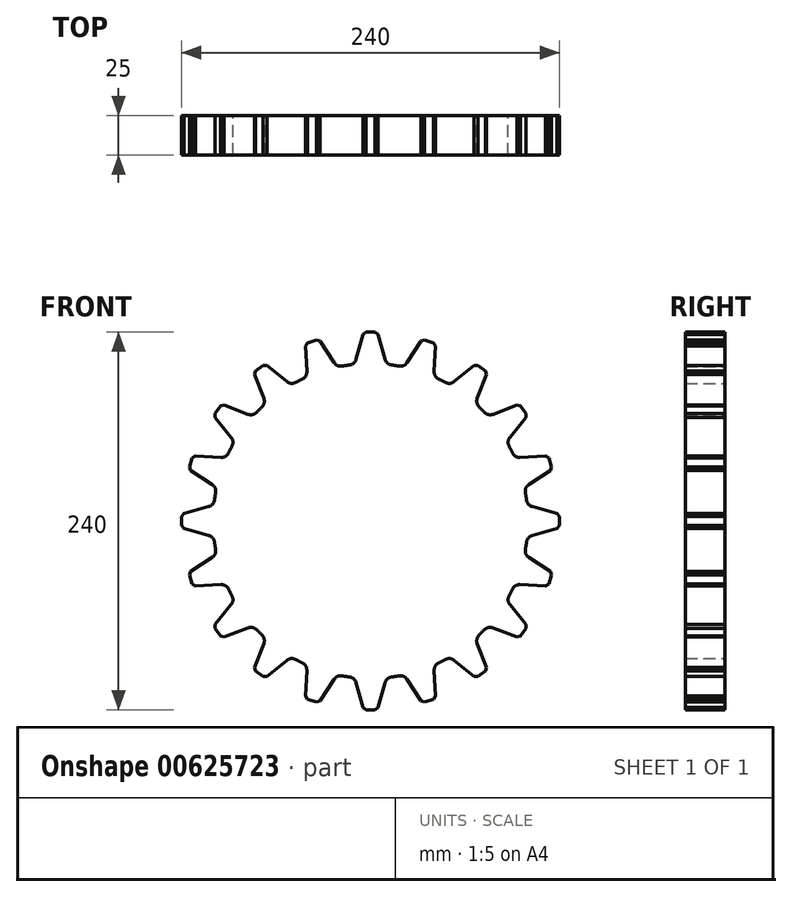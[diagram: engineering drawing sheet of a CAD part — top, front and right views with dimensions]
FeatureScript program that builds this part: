
annotation { "Feature Type Name" : "Feature", "Feature Type Description" : "" }
export const myFeature = defineFeature(function(context is Context, id is Id, definition is map)
    precondition{}
    {
        {
            var Q0;
            Q0=qCreatedBy(makeId("Front.planeOp"),FACE);
            var sketch = newSketch(context, id + "F0", { "sketchPlane" : qUnion([Q0])});
            skCircle(sketch, "E0", {"center": v(0, 0) * mm, "radius": 100 * mm});
            skCircle(sketch, "E1", {"center": v(0, 0) * mm, "radius": 120 * mm, "construction": true});
            skLineSegment(sketch, "E2", {"start": v(0, 120) * mm, "end": v(-4.5, 120) * mm});
            skLineSegment(sketch, "E3", {"start": v(0, 120) * mm, "end": v(4.5, 120) * mm});
            skLineSegment(sketch, "E4", {"start": v(4.5, 120) * mm, "end": v(10, 99.5) * mm});
            skLineSegment(sketch, "E5", {"start": v(-4.5, 120) * mm, "end": v(-10, 99.5) * mm});
            skLineSegment(sketch, "E6.anchor1", {"start": v(0, 0) * mm, "end": v(0, 120) * mm, "construction": true});
            skLineSegment(sketch, "E6.anchor2", {"start": v(0, 0) * mm, "end": v(0, 120) * mm, "construction": true});
            skLineSegment(sketch, "E7.1.0", {"start": v(-37.08, 114.13) * mm, "end": v(-41.36, 112.74) * mm});
            skLineSegment(sketch, "E7.1.1", {"start": v(-37.08, 114.13) * mm, "end": v(-32.8, 115.52) * mm});
            skLineSegment(sketch, "E7.1.2", {"start": v(-32.8, 115.52) * mm, "end": v(-21.24, 97.72) * mm});
            skLineSegment(sketch, "E7.1.3", {"start": v(-41.36, 112.74) * mm, "end": v(-40.25, 91.54) * mm});
            skLineSegment(sketch, "E7.2.0", {"start": v(-70.53, 97.08) * mm, "end": v(-74.17, 94.44) * mm});
            skLineSegment(sketch, "E7.2.1", {"start": v(-70.53, 97.08) * mm, "end": v(-66.9, 99.73) * mm});
            skLineSegment(sketch, "E7.2.2", {"start": v(-66.9, 99.73) * mm, "end": v(-50.4, 86.37) * mm});
            skLineSegment(sketch, "E7.2.3", {"start": v(-74.17, 94.44) * mm, "end": v(-66.57, 74.62) * mm});
            skLineSegment(sketch, "E7.3.0", {"start": v(-97.08, 70.53) * mm, "end": v(-99.73, 66.9) * mm});
            skLineSegment(sketch, "E7.3.1", {"start": v(-97.08, 70.53) * mm, "end": v(-94.44, 74.17) * mm});
            skLineSegment(sketch, "E7.3.2", {"start": v(-94.44, 74.17) * mm, "end": v(-74.62, 66.57) * mm});
            skLineSegment(sketch, "E7.3.3", {"start": v(-99.73, 66.9) * mm, "end": v(-86.37, 50.4) * mm});
            skLineSegment(sketch, "E7.4.0", {"start": v(-114.13, 37.08) * mm, "end": v(-115.52, 32.8) * mm});
            skLineSegment(sketch, "E7.4.1", {"start": v(-114.13, 37.08) * mm, "end": v(-112.74, 41.36) * mm});
            skLineSegment(sketch, "E7.4.2", {"start": v(-112.74, 41.36) * mm, "end": v(-91.54, 40.25) * mm});
            skLineSegment(sketch, "E7.4.3", {"start": v(-115.52, 32.8) * mm, "end": v(-97.72, 21.24) * mm});
            skLineSegment(sketch, "E7.5.0", {"start": v(-120, 0) * mm, "end": v(-120, -4.5) * mm});
            skLineSegment(sketch, "E7.5.1", {"start": v(-120, 0) * mm, "end": v(-120, 4.5) * mm});
            skLineSegment(sketch, "E7.5.2", {"start": v(-120, 4.5) * mm, "end": v(-99.5, 10) * mm});
            skLineSegment(sketch, "E7.5.3", {"start": v(-120, -4.5) * mm, "end": v(-99.5, -10) * mm});
            skLineSegment(sketch, "E7.6.0", {"start": v(-114.13, -37.08) * mm, "end": v(-112.74, -41.36) * mm});
            skLineSegment(sketch, "E7.6.1", {"start": v(-114.13, -37.08) * mm, "end": v(-115.52, -32.8) * mm});
            skLineSegment(sketch, "E7.6.2", {"start": v(-115.52, -32.8) * mm, "end": v(-97.72, -21.24) * mm});
            skLineSegment(sketch, "E7.6.3", {"start": v(-112.74, -41.36) * mm, "end": v(-91.54, -40.25) * mm});
            skLineSegment(sketch, "E7.7.0", {"start": v(-97.08, -70.53) * mm, "end": v(-94.44, -74.17) * mm});
            skLineSegment(sketch, "E7.7.1", {"start": v(-97.08, -70.53) * mm, "end": v(-99.73, -66.9) * mm});
            skLineSegment(sketch, "E7.7.2", {"start": v(-99.73, -66.9) * mm, "end": v(-86.37, -50.4) * mm});
            skLineSegment(sketch, "E7.7.3", {"start": v(-94.44, -74.17) * mm, "end": v(-74.62, -66.57) * mm});
            skLineSegment(sketch, "E7.8.0", {"start": v(-70.53, -97.08) * mm, "end": v(-66.9, -99.73) * mm});
            skLineSegment(sketch, "E7.8.1", {"start": v(-70.53, -97.08) * mm, "end": v(-74.17, -94.44) * mm});
            skLineSegment(sketch, "E7.8.2", {"start": v(-74.17, -94.44) * mm, "end": v(-66.57, -74.62) * mm});
            skLineSegment(sketch, "E7.8.3", {"start": v(-66.9, -99.73) * mm, "end": v(-50.4, -86.37) * mm});
            skLineSegment(sketch, "E7.9.0", {"start": v(-37.08, -114.13) * mm, "end": v(-32.8, -115.52) * mm});
            skLineSegment(sketch, "E7.9.1", {"start": v(-37.08, -114.13) * mm, "end": v(-41.36, -112.74) * mm});
            skLineSegment(sketch, "E7.9.2", {"start": v(-41.36, -112.74) * mm, "end": v(-40.25, -91.54) * mm});
            skLineSegment(sketch, "E7.9.3", {"start": v(-32.8, -115.52) * mm, "end": v(-21.24, -97.72) * mm});
            skLineSegment(sketch, "E7.10.0", {"start": v(0, -120) * mm, "end": v(4.5, -120) * mm});
            skLineSegment(sketch, "E7.10.1", {"start": v(0, -120) * mm, "end": v(-4.5, -120) * mm});
            skLineSegment(sketch, "E7.10.2", {"start": v(-4.5, -120) * mm, "end": v(-10, -99.5) * mm});
            skLineSegment(sketch, "E7.10.3", {"start": v(4.5, -120) * mm, "end": v(10, -99.5) * mm});
            skLineSegment(sketch, "E7.11.0", {"start": v(37.08, -114.13) * mm, "end": v(41.36, -112.74) * mm});
            skLineSegment(sketch, "E7.11.1", {"start": v(37.08, -114.13) * mm, "end": v(32.8, -115.52) * mm});
            skLineSegment(sketch, "E7.11.2", {"start": v(32.8, -115.52) * mm, "end": v(21.24, -97.72) * mm});
            skLineSegment(sketch, "E7.11.3", {"start": v(41.36, -112.74) * mm, "end": v(40.25, -91.54) * mm});
            skLineSegment(sketch, "E7.12.0", {"start": v(70.53, -97.08) * mm, "end": v(74.17, -94.44) * mm});
            skLineSegment(sketch, "E7.12.1", {"start": v(70.53, -97.08) * mm, "end": v(66.9, -99.73) * mm});
            skLineSegment(sketch, "E7.12.2", {"start": v(66.9, -99.73) * mm, "end": v(50.4, -86.37) * mm});
            skLineSegment(sketch, "E7.12.3", {"start": v(74.17, -94.44) * mm, "end": v(66.57, -74.62) * mm});
            skLineSegment(sketch, "E7.13.0", {"start": v(97.08, -70.53) * mm, "end": v(99.73, -66.9) * mm});
            skLineSegment(sketch, "E7.13.1", {"start": v(97.08, -70.53) * mm, "end": v(94.44, -74.17) * mm});
            skLineSegment(sketch, "E7.13.2", {"start": v(94.44, -74.17) * mm, "end": v(74.62, -66.57) * mm});
            skLineSegment(sketch, "E7.13.3", {"start": v(99.73, -66.9) * mm, "end": v(86.37, -50.4) * mm});
            skLineSegment(sketch, "E7.14.0", {"start": v(114.13, -37.08) * mm, "end": v(115.52, -32.8) * mm});
            skLineSegment(sketch, "E7.14.1", {"start": v(114.13, -37.08) * mm, "end": v(112.74, -41.36) * mm});
            skLineSegment(sketch, "E7.14.2", {"start": v(112.74, -41.36) * mm, "end": v(91.54, -40.25) * mm});
            skLineSegment(sketch, "E7.14.3", {"start": v(115.52, -32.8) * mm, "end": v(97.72, -21.24) * mm});
            skLineSegment(sketch, "E7.15.0", {"start": v(120, 0) * mm, "end": v(120, 4.5) * mm});
            skLineSegment(sketch, "E7.15.1", {"start": v(120, 0) * mm, "end": v(120, -4.5) * mm});
            skLineSegment(sketch, "E7.15.2", {"start": v(120, -4.5) * mm, "end": v(99.5, -10) * mm});
            skLineSegment(sketch, "E7.15.3", {"start": v(120, 4.5) * mm, "end": v(99.5, 10) * mm});
            skLineSegment(sketch, "E7.16.0", {"start": v(114.13, 37.08) * mm, "end": v(112.74, 41.36) * mm});
            skLineSegment(sketch, "E7.16.1", {"start": v(114.13, 37.08) * mm, "end": v(115.52, 32.8) * mm});
            skLineSegment(sketch, "E7.16.2", {"start": v(115.52, 32.8) * mm, "end": v(97.72, 21.24) * mm});
            skLineSegment(sketch, "E7.16.3", {"start": v(112.74, 41.36) * mm, "end": v(91.54, 40.25) * mm});
            skLineSegment(sketch, "E7.17.0", {"start": v(97.08, 70.53) * mm, "end": v(94.44, 74.17) * mm});
            skLineSegment(sketch, "E7.17.1", {"start": v(97.08, 70.53) * mm, "end": v(99.73, 66.9) * mm});
            skLineSegment(sketch, "E7.17.2", {"start": v(99.73, 66.9) * mm, "end": v(86.37, 50.4) * mm});
            skLineSegment(sketch, "E7.17.3", {"start": v(94.44, 74.17) * mm, "end": v(74.62, 66.57) * mm});
            skLineSegment(sketch, "E7.18.0", {"start": v(70.53, 97.08) * mm, "end": v(66.9, 99.73) * mm});
            skLineSegment(sketch, "E7.18.1", {"start": v(70.53, 97.08) * mm, "end": v(74.17, 94.44) * mm});
            skLineSegment(sketch, "E7.18.2", {"start": v(74.17, 94.44) * mm, "end": v(66.57, 74.62) * mm});
            skLineSegment(sketch, "E7.18.3", {"start": v(66.9, 99.73) * mm, "end": v(50.4, 86.37) * mm});
            skLineSegment(sketch, "E7.19.0", {"start": v(37.08, 114.13) * mm, "end": v(32.8, 115.52) * mm});
            skLineSegment(sketch, "E7.19.1", {"start": v(37.08, 114.13) * mm, "end": v(41.36, 112.74) * mm});
            skLineSegment(sketch, "E7.19.2", {"start": v(41.36, 112.74) * mm, "end": v(40.25, 91.54) * mm});
            skLineSegment(sketch, "E7.19.3", {"start": v(32.8, 115.52) * mm, "end": v(21.24, 97.72) * mm});
            skSolve(sketch);
        }
        {
            var Q0;
            {var subQ0=sQuery(id+"F0.wireOp",EDGE,"E0");var subQ18=makeQuery(id+"F0.imprint","INTERSECT",VERTEX,{"derivedFrom":[subQ0,sQuery(id+"F0.wireOp",EDGE,"E7.15.3")]});Q0=makeQuery(id+"F0.imprint","IMPRINT",FACE,{"disambiguationData":[TD([[makeQuery(id+"F0.imprint","IMPRINT",EDGE,{"disambiguationData":[TD([[subQ18,-1.0]])],"derivedFrom":subQ0}),1.0]])]});}
            var Q1;
            Q1=makeQuery(id+"F0.imprint","IMPRINT",FACE,{"disambiguationData":[TD([[makeQuery(id+"F0.imprint","IMPRINT",EDGE,{"derivedFrom":sQuery(id+"F0.wireOp",EDGE,"E7.1.0")}),1.0]])]});
            var Q2;
            Q2=makeQuery(id+"F0.imprint","IMPRINT",FACE,{"disambiguationData":[TD([[makeQuery(id+"F0.imprint","IMPRINT",EDGE,{"derivedFrom":sQuery(id+"F0.wireOp",EDGE,"E3")}),-1.0]])]});
            var Q3;
            Q3=makeQuery(id+"F0.imprint","IMPRINT",FACE,{"disambiguationData":[TD([[makeQuery(id+"F0.imprint","IMPRINT",EDGE,{"derivedFrom":sQuery(id+"F0.wireOp",EDGE,"E7.19.0")}),1.0]])]});
            var Q4;
            Q4=makeQuery(id+"F0.imprint","IMPRINT",FACE,{"disambiguationData":[TD([[makeQuery(id+"F0.imprint","IMPRINT",EDGE,{"derivedFrom":sQuery(id+"F0.wireOp",EDGE,"E7.18.0")}),1.0]])]});
            var Q5;
            Q5=makeQuery(id+"F0.imprint","IMPRINT",FACE,{"disambiguationData":[TD([[makeQuery(id+"F0.imprint","IMPRINT",EDGE,{"derivedFrom":sQuery(id+"F0.wireOp",EDGE,"E7.17.0")}),1.0]])]});
            var Q6;
            Q6=makeQuery(id+"F0.imprint","IMPRINT",FACE,{"disambiguationData":[TD([[makeQuery(id+"F0.imprint","IMPRINT",EDGE,{"derivedFrom":sQuery(id+"F0.wireOp",EDGE,"E7.16.0")}),1.0]])]});
            var Q7;
            Q7=makeQuery(id+"F0.imprint","IMPRINT",FACE,{"disambiguationData":[TD([[makeQuery(id+"F0.imprint","IMPRINT",EDGE,{"derivedFrom":sQuery(id+"F0.wireOp",EDGE,"E7.15.0")}),1.0]])]});
            var Q8;
            Q8=makeQuery(id+"F0.imprint","IMPRINT",FACE,{"disambiguationData":[TD([[makeQuery(id+"F0.imprint","IMPRINT",EDGE,{"derivedFrom":sQuery(id+"F0.wireOp",EDGE,"E7.14.0")}),1.0]])]});
            var Q9;
            Q9=makeQuery(id+"F0.imprint","IMPRINT",FACE,{"disambiguationData":[TD([[makeQuery(id+"F0.imprint","IMPRINT",EDGE,{"derivedFrom":sQuery(id+"F0.wireOp",EDGE,"E7.13.0")}),1.0]])]});
            var Q10;
            Q10=makeQuery(id+"F0.imprint","IMPRINT",FACE,{"disambiguationData":[TD([[makeQuery(id+"F0.imprint","IMPRINT",EDGE,{"derivedFrom":sQuery(id+"F0.wireOp",EDGE,"E7.12.0")}),1.0]])]});
            var Q11;
            Q11=makeQuery(id+"F0.imprint","IMPRINT",FACE,{"disambiguationData":[TD([[makeQuery(id+"F0.imprint","IMPRINT",EDGE,{"derivedFrom":sQuery(id+"F0.wireOp",EDGE,"E7.11.0")}),1.0]])]});
            var Q12;
            Q12=makeQuery(id+"F0.imprint","IMPRINT",FACE,{"disambiguationData":[TD([[makeQuery(id+"F0.imprint","IMPRINT",EDGE,{"derivedFrom":sQuery(id+"F0.wireOp",EDGE,"E7.10.0")}),1.0]])]});
            var Q13;
            Q13=makeQuery(id+"F0.imprint","IMPRINT",FACE,{"disambiguationData":[TD([[makeQuery(id+"F0.imprint","IMPRINT",EDGE,{"derivedFrom":sQuery(id+"F0.wireOp",EDGE,"E7.9.0")}),1.0]])]});
            var Q14;
            Q14=makeQuery(id+"F0.imprint","IMPRINT",FACE,{"disambiguationData":[TD([[makeQuery(id+"F0.imprint","IMPRINT",EDGE,{"derivedFrom":sQuery(id+"F0.wireOp",EDGE,"E7.8.0")}),1.0]])]});
            var Q15;
            Q15=makeQuery(id+"F0.imprint","IMPRINT",FACE,{"disambiguationData":[TD([[makeQuery(id+"F0.imprint","IMPRINT",EDGE,{"derivedFrom":sQuery(id+"F0.wireOp",EDGE,"E7.7.0")}),1.0]])]});
            var Q16;
            Q16=makeQuery(id+"F0.imprint","IMPRINT",FACE,{"disambiguationData":[TD([[makeQuery(id+"F0.imprint","IMPRINT",EDGE,{"derivedFrom":sQuery(id+"F0.wireOp",EDGE,"E7.6.0")}),1.0]])]});
            var Q17;
            Q17=makeQuery(id+"F0.imprint","IMPRINT",FACE,{"disambiguationData":[TD([[makeQuery(id+"F0.imprint","IMPRINT",EDGE,{"derivedFrom":sQuery(id+"F0.wireOp",EDGE,"E7.5.0")}),1.0]])]});
            var Q18;
            Q18=makeQuery(id+"F0.imprint","IMPRINT",FACE,{"disambiguationData":[TD([[makeQuery(id+"F0.imprint","IMPRINT",EDGE,{"derivedFrom":sQuery(id+"F0.wireOp",EDGE,"E7.4.0")}),1.0]])]});
            var Q19;
            Q19=makeQuery(id+"F0.imprint","IMPRINT",FACE,{"disambiguationData":[TD([[makeQuery(id+"F0.imprint","IMPRINT",EDGE,{"derivedFrom":sQuery(id+"F0.wireOp",EDGE,"E7.3.0")}),1.0]])]});
            var Q20;
            Q20=makeQuery(id+"F0.imprint","IMPRINT",FACE,{"disambiguationData":[TD([[makeQuery(id+"F0.imprint","IMPRINT",EDGE,{"derivedFrom":sQuery(id+"F0.wireOp",EDGE,"E7.2.0")}),1.0]])]});
            extrude(context, id + "F1", {"entities" : qUnion([Q0, Q1, Q2, Q3, Q4, Q5, Q6, Q7, Q8, Q9, Q10, Q11, Q12, Q13, Q14, Q15, Q16, Q17, Q18, Q19, Q20]), "endBound" : BoundingType.SYMMETRIC, "depth" : 25 * mm, "offsetDistance" : 25 * mm});
        }
        {
            var Q0;
            Q0=makeQuery(id+"F1.opExtrude","SWEPT_EDGE",EDGE,{"disambiguationData":[OSD([sQuery(id+"F0.wireOp",EDGE,"E7.15.1"),sQuery(id+"F0.wireOp",EDGE,"E7.15.2")])]});
            var Q1;
            Q1=makeQuery(id+"F1.opExtrude","SWEPT_EDGE",EDGE,{"disambiguationData":[OSD([sQuery(id+"F0.wireOp",EDGE,"E7.15.0"),sQuery(id+"F0.wireOp",EDGE,"E7.15.3")])]});
            chamfer(context, id + "F2", {"entities" : qUnion([Q0, Q1]), "width" : 2 * mm, "tangentPropagation" : true});
        }
        {
            var Q0;
            Q0=makeQuery(id+"F1.opExtrude","SWEPT_EDGE",EDGE,{"disambiguationData":[OSD([sQuery(id+"F0.wireOp",EDGE,"E0"),sQuery(id+"F0.wireOp",EDGE,"E7.15.3")])]});
            var Q1;
            Q1=makeQuery(id+"F1.opExtrude","SWEPT_EDGE",EDGE,{"disambiguationData":[OSD([sQuery(id+"F0.wireOp",EDGE,"E0"),sQuery(id+"F0.wireOp",EDGE,"E7.16.2")])]});
            fillet(context, id + "F3", {"entities" : qUnion([Q0, Q1]), "radius" : 5 * mm, "tangentPropagation" : true, "allowEdgeOverflow" : false});
        }
        {
            var Q0;
            Q0=makeQuery(id+"F1.opExtrude","SWEPT_EDGE",EDGE,{"disambiguationData":[OSD([sQuery(id+"F0.wireOp",EDGE,"E7.14.0"),sQuery(id+"F0.wireOp",EDGE,"E7.14.3")])]});
            var Q1;
            Q1=makeQuery(id+"F1.opExtrude","SWEPT_EDGE",EDGE,{"disambiguationData":[OSD([sQuery(id+"F0.wireOp",EDGE,"E7.14.1"),sQuery(id+"F0.wireOp",EDGE,"E7.14.2")])]});
            var Q2;
            Q2=makeQuery(id+"F1.opExtrude","SWEPT_EDGE",EDGE,{"disambiguationData":[OSD([sQuery(id+"F0.wireOp",EDGE,"E7.13.0"),sQuery(id+"F0.wireOp",EDGE,"E7.13.3")])]});
            var Q3;
            Q3=makeQuery(id+"F1.opExtrude","SWEPT_EDGE",EDGE,{"disambiguationData":[OSD([sQuery(id+"F0.wireOp",EDGE,"E7.13.1"),sQuery(id+"F0.wireOp",EDGE,"E7.13.2")])]});
            var Q4;
            Q4=makeQuery(id+"F1.opExtrude","SWEPT_EDGE",EDGE,{"disambiguationData":[OSD([sQuery(id+"F0.wireOp",EDGE,"E7.12.0"),sQuery(id+"F0.wireOp",EDGE,"E7.12.3")])]});
            var Q5;
            Q5=makeQuery(id+"F1.opExtrude","SWEPT_EDGE",EDGE,{"disambiguationData":[OSD([sQuery(id+"F0.wireOp",EDGE,"E7.12.1"),sQuery(id+"F0.wireOp",EDGE,"E7.12.2")])]});
            var Q6;
            Q6=makeQuery(id+"F1.opExtrude","SWEPT_EDGE",EDGE,{"disambiguationData":[OSD([sQuery(id+"F0.wireOp",EDGE,"E7.11.0"),sQuery(id+"F0.wireOp",EDGE,"E7.11.3")])]});
            var Q7;
            Q7=makeQuery(id+"F1.opExtrude","SWEPT_EDGE",EDGE,{"disambiguationData":[OSD([sQuery(id+"F0.wireOp",EDGE,"E7.11.1"),sQuery(id+"F0.wireOp",EDGE,"E7.11.2")])]});
            var Q8;
            Q8=makeQuery(id+"F1.opExtrude","SWEPT_EDGE",EDGE,{"disambiguationData":[OSD([sQuery(id+"F0.wireOp",EDGE,"E7.10.0"),sQuery(id+"F0.wireOp",EDGE,"E7.10.3")])]});
            var Q9;
            Q9=makeQuery(id+"F1.opExtrude","SWEPT_EDGE",EDGE,{"disambiguationData":[OSD([sQuery(id+"F0.wireOp",EDGE,"E7.10.1"),sQuery(id+"F0.wireOp",EDGE,"E7.10.2")])]});
            var Q10;
            Q10=makeQuery(id+"F1.opExtrude","SWEPT_EDGE",EDGE,{"disambiguationData":[OSD([sQuery(id+"F0.wireOp",EDGE,"E7.9.0"),sQuery(id+"F0.wireOp",EDGE,"E7.9.3")])]});
            var Q11;
            Q11=makeQuery(id+"F1.opExtrude","SWEPT_EDGE",EDGE,{"disambiguationData":[OSD([sQuery(id+"F0.wireOp",EDGE,"E7.9.1"),sQuery(id+"F0.wireOp",EDGE,"E7.9.2")])]});
            var Q12;
            Q12=makeQuery(id+"F1.opExtrude","SWEPT_EDGE",EDGE,{"disambiguationData":[OSD([sQuery(id+"F0.wireOp",EDGE,"E7.8.0"),sQuery(id+"F0.wireOp",EDGE,"E7.8.3")])]});
            var Q13;
            Q13=makeQuery(id+"F1.opExtrude","SWEPT_EDGE",EDGE,{"disambiguationData":[OSD([sQuery(id+"F0.wireOp",EDGE,"E7.8.1"),sQuery(id+"F0.wireOp",EDGE,"E7.8.2")])]});
            var Q14;
            Q14=makeQuery(id+"F1.opExtrude","SWEPT_EDGE",EDGE,{"disambiguationData":[OSD([sQuery(id+"F0.wireOp",EDGE,"E7.7.0"),sQuery(id+"F0.wireOp",EDGE,"E7.7.3")])]});
            var Q15;
            Q15=makeQuery(id+"F1.opExtrude","SWEPT_EDGE",EDGE,{"disambiguationData":[OSD([sQuery(id+"F0.wireOp",EDGE,"E7.7.1"),sQuery(id+"F0.wireOp",EDGE,"E7.7.2")])]});
            var Q16;
            Q16=makeQuery(id+"F1.opExtrude","SWEPT_EDGE",EDGE,{"disambiguationData":[OSD([sQuery(id+"F0.wireOp",EDGE,"E7.6.0"),sQuery(id+"F0.wireOp",EDGE,"E7.6.3")])]});
            var Q17;
            Q17=makeQuery(id+"F1.opExtrude","SWEPT_EDGE",EDGE,{"disambiguationData":[OSD([sQuery(id+"F0.wireOp",EDGE,"E7.6.1"),sQuery(id+"F0.wireOp",EDGE,"E7.6.2")])]});
            var Q18;
            Q18=makeQuery(id+"F1.opExtrude","SWEPT_EDGE",EDGE,{"disambiguationData":[OSD([sQuery(id+"F0.wireOp",EDGE,"E7.5.0"),sQuery(id+"F0.wireOp",EDGE,"E7.5.3")])]});
            var Q19;
            Q19=makeQuery(id+"F1.opExtrude","SWEPT_EDGE",EDGE,{"disambiguationData":[OSD([sQuery(id+"F0.wireOp",EDGE,"E7.5.1"),sQuery(id+"F0.wireOp",EDGE,"E7.5.2")])]});
            var Q20;
            Q20=makeQuery(id+"F1.opExtrude","SWEPT_EDGE",EDGE,{"disambiguationData":[OSD([sQuery(id+"F0.wireOp",EDGE,"E7.4.0"),sQuery(id+"F0.wireOp",EDGE,"E7.4.3")])]});
            var Q21;
            Q21=makeQuery(id+"F1.opExtrude","SWEPT_EDGE",EDGE,{"disambiguationData":[OSD([sQuery(id+"F0.wireOp",EDGE,"E7.4.1"),sQuery(id+"F0.wireOp",EDGE,"E7.4.2")])]});
            var Q22;
            Q22=makeQuery(id+"F1.opExtrude","SWEPT_EDGE",EDGE,{"disambiguationData":[OSD([sQuery(id+"F0.wireOp",EDGE,"E7.3.0"),sQuery(id+"F0.wireOp",EDGE,"E7.3.3")])]});
            var Q23;
            Q23=makeQuery(id+"F1.opExtrude","SWEPT_EDGE",EDGE,{"disambiguationData":[OSD([sQuery(id+"F0.wireOp",EDGE,"E7.3.1"),sQuery(id+"F0.wireOp",EDGE,"E7.3.2")])]});
            var Q24;
            Q24=makeQuery(id+"F1.opExtrude","SWEPT_EDGE",EDGE,{"disambiguationData":[OSD([sQuery(id+"F0.wireOp",EDGE,"E7.2.0"),sQuery(id+"F0.wireOp",EDGE,"E7.2.3")])]});
            var Q25;
            Q25=makeQuery(id+"F1.opExtrude","SWEPT_EDGE",EDGE,{"disambiguationData":[OSD([sQuery(id+"F0.wireOp",EDGE,"E7.2.1"),sQuery(id+"F0.wireOp",EDGE,"E7.2.2")])]});
            var Q26;
            Q26=makeQuery(id+"F1.opExtrude","SWEPT_EDGE",EDGE,{"disambiguationData":[OSD([sQuery(id+"F0.wireOp",EDGE,"E7.1.0"),sQuery(id+"F0.wireOp",EDGE,"E7.1.3")])]});
            var Q27;
            Q27=makeQuery(id+"F1.opExtrude","SWEPT_EDGE",EDGE,{"disambiguationData":[OSD([sQuery(id+"F0.wireOp",EDGE,"E7.1.1"),sQuery(id+"F0.wireOp",EDGE,"E7.1.2")])]});
            var Q28;
            Q28=makeQuery(id+"F1.opExtrude","SWEPT_EDGE",EDGE,{"disambiguationData":[OSD([sQuery(id+"F0.wireOp",EDGE,"E2"),sQuery(id+"F0.wireOp",EDGE,"E5")])]});
            var Q29;
            Q29=makeQuery(id+"F1.opExtrude","SWEPT_EDGE",EDGE,{"disambiguationData":[OSD([sQuery(id+"F0.wireOp",EDGE,"E3"),sQuery(id+"F0.wireOp",EDGE,"E4")])]});
            var Q30;
            Q30=makeQuery(id+"F1.opExtrude","SWEPT_EDGE",EDGE,{"disambiguationData":[OSD([sQuery(id+"F0.wireOp",EDGE,"E7.19.0"),sQuery(id+"F0.wireOp",EDGE,"E7.19.3")])]});
            var Q31;
            Q31=makeQuery(id+"F1.opExtrude","SWEPT_EDGE",EDGE,{"disambiguationData":[OSD([sQuery(id+"F0.wireOp",EDGE,"E7.19.1"),sQuery(id+"F0.wireOp",EDGE,"E7.19.2")])]});
            var Q32;
            Q32=makeQuery(id+"F1.opExtrude","SWEPT_EDGE",EDGE,{"disambiguationData":[OSD([sQuery(id+"F0.wireOp",EDGE,"E7.18.0"),sQuery(id+"F0.wireOp",EDGE,"E7.18.3")])]});
            var Q33;
            Q33=makeQuery(id+"F1.opExtrude","SWEPT_EDGE",EDGE,{"disambiguationData":[OSD([sQuery(id+"F0.wireOp",EDGE,"E7.18.1"),sQuery(id+"F0.wireOp",EDGE,"E7.18.2")])]});
            var Q34;
            Q34=makeQuery(id+"F1.opExtrude","SWEPT_EDGE",EDGE,{"disambiguationData":[OSD([sQuery(id+"F0.wireOp",EDGE,"E7.17.0"),sQuery(id+"F0.wireOp",EDGE,"E7.17.3")])]});
            var Q35;
            Q35=makeQuery(id+"F1.opExtrude","SWEPT_EDGE",EDGE,{"disambiguationData":[OSD([sQuery(id+"F0.wireOp",EDGE,"E7.17.1"),sQuery(id+"F0.wireOp",EDGE,"E7.17.2")])]});
            var Q36;
            Q36=makeQuery(id+"F1.opExtrude","SWEPT_EDGE",EDGE,{"disambiguationData":[OSD([sQuery(id+"F0.wireOp",EDGE,"E7.16.0"),sQuery(id+"F0.wireOp",EDGE,"E7.16.3")])]});
            var Q37;
            Q37=makeQuery(id+"F1.opExtrude","SWEPT_EDGE",EDGE,{"disambiguationData":[OSD([sQuery(id+"F0.wireOp",EDGE,"E7.16.1"),sQuery(id+"F0.wireOp",EDGE,"E7.16.2")])]});
            chamfer(context, id + "F4", {"entities" : qUnion([Q0, Q1, Q2, Q3, Q4, Q5, Q6, Q7, Q8, Q9, Q10, Q11, Q12, Q13, Q14, Q15, Q16, Q17, Q18, Q19, Q20, Q21, Q22, Q23, Q24, Q25, Q26, Q27, Q28, Q29, Q30, Q31, Q32, Q33, Q34, Q35, Q36, Q37]), "width" : 2 * mm, "tangentPropagation" : true});
        }
        {
            var Q0;
            Q0=makeQuery(id+"F1.opExtrude","SWEPT_EDGE",EDGE,{"disambiguationData":[OSD([sQuery(id+"F0.wireOp",EDGE,"E0"),sQuery(id+"F0.wireOp",EDGE,"E7.17.2")])]});
            var Q1;
            Q1=makeQuery(id+"F1.opExtrude","SWEPT_EDGE",EDGE,{"disambiguationData":[OSD([sQuery(id+"F0.wireOp",EDGE,"E0"),sQuery(id+"F0.wireOp",EDGE,"E7.16.3")])]});
            var Q2;
            Q2=makeQuery(id+"F1.opExtrude","SWEPT_EDGE",EDGE,{"disambiguationData":[OSD([sQuery(id+"F0.wireOp",EDGE,"E0"),sQuery(id+"F0.wireOp",EDGE,"E7.15.2")])]});
            var Q3;
            Q3=makeQuery(id+"F1.opExtrude","SWEPT_EDGE",EDGE,{"disambiguationData":[OSD([sQuery(id+"F0.wireOp",EDGE,"E0"),sQuery(id+"F0.wireOp",EDGE,"E7.14.3")])]});
            var Q4;
            Q4=makeQuery(id+"F1.opExtrude","SWEPT_EDGE",EDGE,{"disambiguationData":[OSD([sQuery(id+"F0.wireOp",EDGE,"E0"),sQuery(id+"F0.wireOp",EDGE,"E7.14.2")])]});
            var Q5;
            Q5=makeQuery(id+"F1.opExtrude","SWEPT_EDGE",EDGE,{"disambiguationData":[OSD([sQuery(id+"F0.wireOp",EDGE,"E0"),sQuery(id+"F0.wireOp",EDGE,"E7.13.3")])]});
            var Q6;
            Q6=makeQuery(id+"F1.opExtrude","SWEPT_EDGE",EDGE,{"disambiguationData":[OSD([sQuery(id+"F0.wireOp",EDGE,"E0"),sQuery(id+"F0.wireOp",EDGE,"E7.13.2")])]});
            var Q7;
            Q7=makeQuery(id+"F1.opExtrude","SWEPT_EDGE",EDGE,{"disambiguationData":[OSD([sQuery(id+"F0.wireOp",EDGE,"E0"),sQuery(id+"F0.wireOp",EDGE,"E7.12.3")])]});
            var Q8;
            Q8=makeQuery(id+"F1.opExtrude","SWEPT_EDGE",EDGE,{"disambiguationData":[OSD([sQuery(id+"F0.wireOp",EDGE,"E0"),sQuery(id+"F0.wireOp",EDGE,"E7.12.2")])]});
            var Q9;
            Q9=makeQuery(id+"F1.opExtrude","SWEPT_EDGE",EDGE,{"disambiguationData":[OSD([sQuery(id+"F0.wireOp",EDGE,"E0"),sQuery(id+"F0.wireOp",EDGE,"E7.11.3")])]});
            var Q10;
            Q10=makeQuery(id+"F1.opExtrude","SWEPT_EDGE",EDGE,{"disambiguationData":[OSD([sQuery(id+"F0.wireOp",EDGE,"E0"),sQuery(id+"F0.wireOp",EDGE,"E7.10.2")])]});
            var Q11;
            Q11=makeQuery(id+"F1.opExtrude","SWEPT_EDGE",EDGE,{"disambiguationData":[OSD([sQuery(id+"F0.wireOp",EDGE,"E0"),sQuery(id+"F0.wireOp",EDGE,"E7.9.3")])]});
            var Q12;
            Q12=makeQuery(id+"F1.opExtrude","SWEPT_EDGE",EDGE,{"disambiguationData":[OSD([sQuery(id+"F0.wireOp",EDGE,"E0"),sQuery(id+"F0.wireOp",EDGE,"E7.9.2")])]});
            var Q13;
            Q13=makeQuery(id+"F1.opExtrude","SWEPT_EDGE",EDGE,{"disambiguationData":[OSD([sQuery(id+"F0.wireOp",EDGE,"E0"),sQuery(id+"F0.wireOp",EDGE,"E7.8.3")])]});
            var Q14;
            Q14=makeQuery(id+"F1.opExtrude","SWEPT_EDGE",EDGE,{"disambiguationData":[OSD([sQuery(id+"F0.wireOp",EDGE,"E0"),sQuery(id+"F0.wireOp",EDGE,"E7.8.2")])]});
            var Q15;
            Q15=makeQuery(id+"F1.opExtrude","SWEPT_EDGE",EDGE,{"disambiguationData":[OSD([sQuery(id+"F0.wireOp",EDGE,"E0"),sQuery(id+"F0.wireOp",EDGE,"E7.7.3")])]});
            var Q16;
            Q16=makeQuery(id+"F1.opExtrude","SWEPT_EDGE",EDGE,{"disambiguationData":[OSD([sQuery(id+"F0.wireOp",EDGE,"E0"),sQuery(id+"F0.wireOp",EDGE,"E7.7.2")])]});
            var Q17;
            Q17=makeQuery(id+"F1.opExtrude","SWEPT_EDGE",EDGE,{"disambiguationData":[OSD([sQuery(id+"F0.wireOp",EDGE,"E0"),sQuery(id+"F0.wireOp",EDGE,"E7.6.3")])]});
            var Q18;
            Q18=makeQuery(id+"F1.opExtrude","SWEPT_EDGE",EDGE,{"disambiguationData":[OSD([sQuery(id+"F0.wireOp",EDGE,"E0"),sQuery(id+"F0.wireOp",EDGE,"E7.6.2")])]});
            var Q19;
            Q19=makeQuery(id+"F1.opExtrude","SWEPT_EDGE",EDGE,{"disambiguationData":[OSD([sQuery(id+"F0.wireOp",EDGE,"E0"),sQuery(id+"F0.wireOp",EDGE,"E7.5.3")])]});
            var Q20;
            Q20=makeQuery(id+"F1.opExtrude","SWEPT_EDGE",EDGE,{"disambiguationData":[OSD([sQuery(id+"F0.wireOp",EDGE,"E0"),sQuery(id+"F0.wireOp",EDGE,"E7.5.2")])]});
            var Q21;
            Q21=makeQuery(id+"F1.opExtrude","SWEPT_EDGE",EDGE,{"disambiguationData":[OSD([sQuery(id+"F0.wireOp",EDGE,"E0"),sQuery(id+"F0.wireOp",EDGE,"E7.4.3")])]});
            var Q22;
            Q22=makeQuery(id+"F1.opExtrude","SWEPT_EDGE",EDGE,{"disambiguationData":[OSD([sQuery(id+"F0.wireOp",EDGE,"E0"),sQuery(id+"F0.wireOp",EDGE,"E7.4.2")])]});
            var Q23;
            Q23=makeQuery(id+"F1.opExtrude","SWEPT_EDGE",EDGE,{"disambiguationData":[OSD([sQuery(id+"F0.wireOp",EDGE,"E0"),sQuery(id+"F0.wireOp",EDGE,"E7.3.3")])]});
            var Q24;
            Q24=makeQuery(id+"F1.opExtrude","SWEPT_EDGE",EDGE,{"disambiguationData":[OSD([sQuery(id+"F0.wireOp",EDGE,"E0"),sQuery(id+"F0.wireOp",EDGE,"E7.3.2")])]});
            var Q25;
            Q25=makeQuery(id+"F1.opExtrude","SWEPT_EDGE",EDGE,{"disambiguationData":[OSD([sQuery(id+"F0.wireOp",EDGE,"E0"),sQuery(id+"F0.wireOp",EDGE,"E7.2.3")])]});
            var Q26;
            Q26=makeQuery(id+"F1.opExtrude","SWEPT_EDGE",EDGE,{"disambiguationData":[OSD([sQuery(id+"F0.wireOp",EDGE,"E0"),sQuery(id+"F0.wireOp",EDGE,"E7.2.2")])]});
            var Q27;
            Q27=makeQuery(id+"F1.opExtrude","SWEPT_EDGE",EDGE,{"disambiguationData":[OSD([sQuery(id+"F0.wireOp",EDGE,"E0"),sQuery(id+"F0.wireOp",EDGE,"E7.1.3")])]});
            var Q28;
            Q28=makeQuery(id+"F1.opExtrude","SWEPT_EDGE",EDGE,{"disambiguationData":[OSD([sQuery(id+"F0.wireOp",EDGE,"E0"),sQuery(id+"F0.wireOp",EDGE,"E7.1.2")])]});
            var Q29;
            Q29=makeQuery(id+"F1.opExtrude","SWEPT_EDGE",EDGE,{"disambiguationData":[OSD([sQuery(id+"F0.wireOp",EDGE,"E0"),sQuery(id+"F0.wireOp",EDGE,"E5")])]});
            var Q30;
            Q30=makeQuery(id+"F1.opExtrude","SWEPT_EDGE",EDGE,{"disambiguationData":[OSD([sQuery(id+"F0.wireOp",EDGE,"E0"),sQuery(id+"F0.wireOp",EDGE,"E4")])]});
            var Q31;
            Q31=makeQuery(id+"F1.opExtrude","SWEPT_EDGE",EDGE,{"disambiguationData":[OSD([sQuery(id+"F0.wireOp",EDGE,"E0"),sQuery(id+"F0.wireOp",EDGE,"E7.19.3")])]});
            var Q32;
            Q32=makeQuery(id+"F1.opExtrude","SWEPT_EDGE",EDGE,{"disambiguationData":[OSD([sQuery(id+"F0.wireOp",EDGE,"E0"),sQuery(id+"F0.wireOp",EDGE,"E7.19.2")])]});
            var Q33;
            Q33=makeQuery(id+"F1.opExtrude","SWEPT_EDGE",EDGE,{"disambiguationData":[OSD([sQuery(id+"F0.wireOp",EDGE,"E0"),sQuery(id+"F0.wireOp",EDGE,"E7.18.3")])]});
            var Q34;
            Q34=makeQuery(id+"F1.opExtrude","SWEPT_EDGE",EDGE,{"disambiguationData":[OSD([sQuery(id+"F0.wireOp",EDGE,"E0"),sQuery(id+"F0.wireOp",EDGE,"E7.18.2")])]});
            var Q35;
            Q35=makeQuery(id+"F1.opExtrude","SWEPT_EDGE",EDGE,{"disambiguationData":[OSD([sQuery(id+"F0.wireOp",EDGE,"E0"),sQuery(id+"F0.wireOp",EDGE,"E7.17.3")])]});
            fillet(context, id + "F5", {"entities" : qUnion([Q0, Q1, Q2, Q3, Q4, Q5, Q6, Q7, Q8, Q9, Q10, Q11, Q12, Q13, Q14, Q15, Q16, Q17, Q18, Q19, Q20, Q21, Q22, Q23, Q24, Q25, Q26, Q27, Q28, Q29, Q30, Q31, Q32, Q33, Q34, Q35]), "radius" : 5 * mm, "tangentPropagation" : true, "allowEdgeOverflow" : false});
        }
    });
